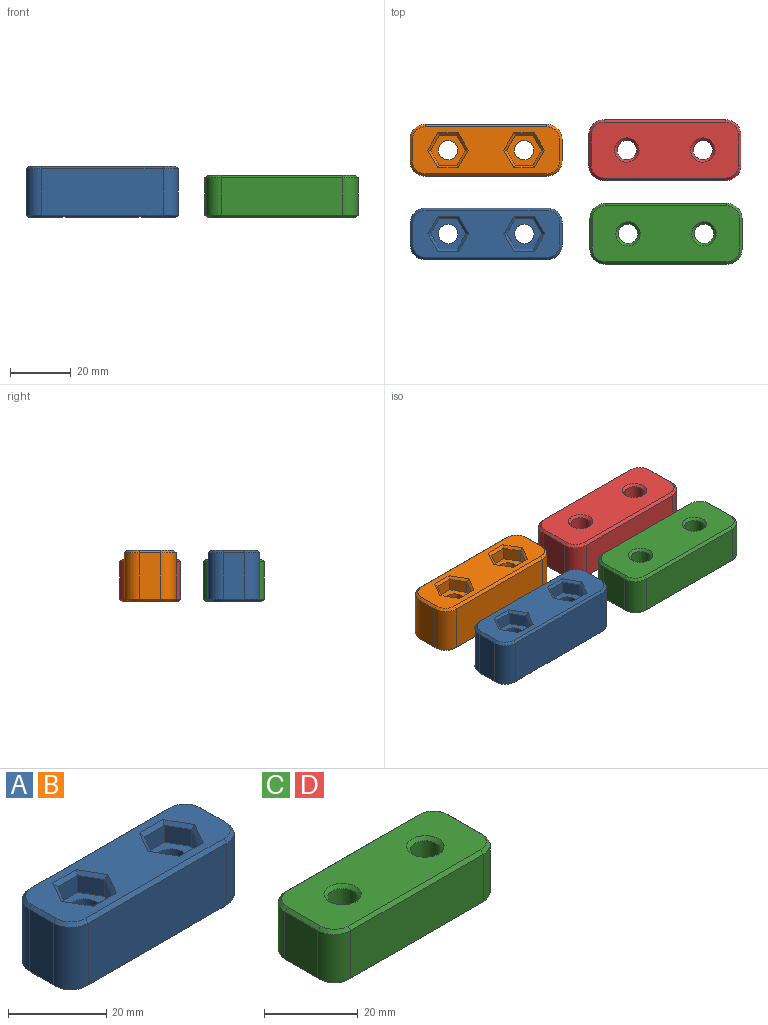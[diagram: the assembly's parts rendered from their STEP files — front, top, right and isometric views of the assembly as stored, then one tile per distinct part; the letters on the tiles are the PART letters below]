
ASSEMBLY  parts=4 mates=3
PART A: 62 faces, bbox 50x17x17 mm
  f0: plane 15.4x8.6mm, normal (0,0,-1), area 66.9mm2, adj f53,f57,f58,f59,f60,f61
  f1: plane 15.4x8.6mm, normal (0,0,-1), area 66.9mm2, adj f52,f54,f55,f56,f57,f58
  f2: cylinder r=3.2mm len=6.4mm, axis (0,0,-1), area 100.5mm2, adj f11,f27
  f3: cylinder r=3.2mm len=6.4mm, axis (0,0,-1), area 100.5mm2, adj f13,f20
  f4: plane 40x15.4mm, normal (0,1,0), area 616mm2, adj f28,f31,f35,f57
  f5: plane 15.4x7mm, normal (-1,0,0), area 107.8mm2, adj f28,f29,f32,f52
  f6: plane 40x15.4mm, normal (0,-1,0), area 616mm2, adj f29,f30,f36,f58
  f7: plane 15.4x7mm, normal (1,0,0), area 107.8mm2, adj f30,f31,f39,f61
  f8: plane 48.4x15.4mm, normal (0,0,1), area 497.2mm2, adj f32,f33,f34,f35,f36,f37,f38,f39
  f9: plane 18.8x15.4mm, normal (0,0,-1), area 173.6mm2, adj f53,f55,f57,f58
  f10: cylinder r=7.5mm len=15mm, axis (0,0,-1), area 292.2mm2, adj f11,f55
  f11: plane 15x15mm, normal (0,0,-1), area 144.5mm2, adj f2,f10
  f12: cylinder r=7.5mm len=15mm, axis (0,0,-1), area 292.2mm2, adj f13,f53
  f13: plane 15x15mm, normal (0,0,-1), area 144.5mm2, adj f3,f12
  f14: plane 5x4.2mm, normal (-0.87,-0.5,0), area 24.2mm2, adj f15,f19,f20,f45
  f15: plane 5.77x4.2mm, normal (0,-1,0), area 24.2mm2, adj f14,f16,f20,f44
  f16: plane 5x4.2mm, normal (0.87,-0.5,0), area 24.2mm2, adj f15,f17,f20,f42
  f17: plane 5x4.2mm, normal (0.87,0.5,0), area 24.2mm2, adj f16,f18,f20,f40
  f18: plane 5.77x4.2mm, normal (0,1,0), area 24.2mm2, adj f17,f19,f20,f41
  f19: plane 5x4.2mm, normal (-0.87,0.5,0), area 24.2mm2, adj f14,f18,f20,f43
  f20: plane 11.55x10mm, normal (0,0,1), area 54.4mm2, adj f3,f14,f15,f16,f17,f18,f19
  f21: plane 5x4.2mm, normal (-0.87,-0.5,0), area 24.2mm2, adj f22,f26,f27,f51
  f22: plane 5.77x4.2mm, normal (0,-1,0), area 24.2mm2, adj f21,f23,f27,f50
  f23: plane 5x4.2mm, normal (0.87,-0.5,0), area 24.2mm2, adj f22,f24,f27,f48
  f24: plane 5x4.2mm, normal (0.87,0.5,0), area 24.2mm2, adj f23,f25,f27,f46
  f25: plane 5.77x4.2mm, normal (0,1,0), area 24.2mm2, adj f24,f26,f27,f47
  f26: plane 5x4.2mm, normal (-0.87,0.5,0), area 24.2mm2, adj f21,f25,f27,f49
  f27: plane 11.55x10mm, normal (0,0,1), area 54.4mm2, adj f2,f21,f22,f23,f24,f25,f26
  f28: cylinder r=5mm len=15.4mm, axis (0,0,1), area 121mm2, adj f4,f5,f33,f54
  f29: cylinder r=5mm len=15.4mm, axis (0,0,-1), area 121mm2, adj f5,f6,f34,f56
  f30: cylinder r=5mm len=15.4mm, axis (0,0,1), area 121mm2, adj f6,f7,f38,f60
  f31: cylinder r=5mm len=15.4mm, axis (0,0,-1), area 121mm2, adj f4,f7,f37,f59
  f32: plane 7x0.8mm, normal (-0.71,0,0.71), area 7.9mm2, adj f5,f8,f33,f34
  f33: cone r=4.2mm half-angle=45deg, axis (0,0,-1), area 8.2mm2, adj f8,f28,f32,f35
  f34: cone r=4.2mm half-angle=45deg, axis (0,0,-1), area 8.2mm2, adj f8,f29,f32,f36
  f35: plane 40x0.8mm, normal (0,0.71,0.71), area 45.3mm2, adj f4,f8,f33,f37
  f36: plane 40x0.8mm, normal (0,-0.71,0.71), area 45.3mm2, adj f6,f8,f34,f38
  f37: cone r=4.2mm half-angle=45deg, axis (0,0,-1), area 8.2mm2, adj f8,f31,f35,f39
  f38: cone r=4.2mm half-angle=45deg, axis (0,0,-1), area 8.2mm2, adj f8,f30,f36,f39
  f39: plane 7x0.8mm, normal (0.71,0,0.71), area 7.9mm2, adj f7,f8,f37,f38
  f40: plane 5.8x3.81mm, normal (0.61,0.35,0.71), area 7.1mm2, adj f8,f17,f41,f42
  f41: plane 6.7x0.8mm, normal (0,0.71,0.71), area 7.1mm2, adj f8,f18,f40,f43
  f42: plane 5.8x3.81mm, normal (0.61,-0.35,0.71), area 7.1mm2, adj f8,f16,f40,f44
  f43: plane 5.8x3.81mm, normal (-0.61,0.35,0.71), area 7.1mm2, adj f8,f19,f41,f45
  f44: plane 6.7x0.8mm, normal (0,-0.71,0.71), area 7.1mm2, adj f8,f15,f42,f45
  f45: plane 5.8x3.81mm, normal (-0.61,-0.35,0.71), area 7.1mm2, adj f8,f14,f43,f44
  f46: plane 5.8x3.81mm, normal (0.61,0.35,0.71), area 7.1mm2, adj f8,f24,f47,f48
  f47: plane 6.7x0.8mm, normal (0,0.71,0.71), area 7.1mm2, adj f8,f25,f46,f49
  f48: plane 5.8x3.81mm, normal (0.61,-0.35,0.71), area 7.1mm2, adj f8,f23,f46,f50
  f49: plane 5.8x3.81mm, normal (-0.61,0.35,0.71), area 7.1mm2, adj f8,f26,f47,f51
  f50: plane 6.7x0.8mm, normal (0,-0.71,0.71), area 7.1mm2, adj f8,f22,f48,f51
  f51: plane 5.8x3.81mm, normal (-0.61,-0.35,0.71), area 7.1mm2, adj f8,f21,f49,f50
  f52: plane 7x0.8mm, normal (-0.71,0,-0.71), area 7.9mm2, adj f1,f5,f54,f56
  f53: cone r=8.3mm half-angle=45deg, axis (0,0,-1), area 52.6mm2, adj f0,f9,f12,f57,f58
  f54: cone r=4.2mm half-angle=45deg, axis (0,0,1), area 8.2mm2, adj f1,f28,f52,f57
  f55: cone r=8.3mm half-angle=45deg, axis (0,0,-1), area 52.6mm2, adj f1,f9,f10,f57,f58
  f56: cone r=4.2mm half-angle=45deg, axis (0,0,1), area 8.2mm2, adj f1,f29,f52,f58
  f57: plane 40x0.81mm, normal (0,0.71,-0.71), area 41.7mm2, adj f0,f1,f4,f9,f53,f54,f55,f59
  f58: plane 40x0.8mm, normal (0,-0.71,-0.71), area 41.7mm2, adj f0,f1,f6,f9,f53,f55,f56,f60
  f59: cone r=4.2mm half-angle=45deg, axis (0,0,1), area 8.2mm2, adj f0,f31,f57,f61
  f60: cone r=4.2mm half-angle=45deg, axis (0,0,1), area 8.2mm2, adj f0,f30,f58,f61
  f61: plane 7x0.8mm, normal (0.71,0,-0.71), area 7.9mm2, adj f0,f7,f59,f60
PART B: same geometry as A
PART C: 32 faces, bbox 50x20x14 mm
  f0: plane 40x12.4mm, normal (0,1,0), area 496mm2, adj f8,f11,f15,f25
  f1: plane 12.4x10mm, normal (-1,0,0), area 124mm2, adj f8,f9,f12,f22
  f2: plane 40x12.4mm, normal (0,-1,0), area 496mm2, adj f9,f10,f16,f26
  f3: cylinder r=3.2mm len=12.4mm, axis (0,0,-1), area 249.3mm2, adj f21,f31
  f4: cylinder r=3.2mm len=12.4mm, axis (0,0,-1), area 249.3mm2, adj f20,f30
  f5: plane 12.4x10mm, normal (1,0,0), area 124mm2, adj f10,f11,f19,f29
  f6: plane 48.4x18.4mm, normal (0,0,1), area 774.9mm2, adj f22,f23,f24,f25,f26,f27,f28,f29
  f7: plane 48.4x18.4mm, normal (0,0,-1), area 774.9mm2, adj f12,f13,f14,f15,f16,f17,f18,f19
  f8: cylinder r=5mm len=12.4mm, axis (0,0,1), area 97.4mm2, adj f0,f1,f13,f23
  f9: cylinder r=5mm len=12.4mm, axis (0,0,-1), area 97.4mm2, adj f1,f2,f14,f24
  f10: cylinder r=5mm len=12.4mm, axis (0,0,1), area 97.4mm2, adj f2,f5,f18,f28
  f11: cylinder r=5mm len=12.4mm, axis (0,0,-1), area 97.4mm2, adj f0,f5,f17,f27
  f12: plane 10x0.8mm, normal (-0.71,0,-0.71), area 11.3mm2, adj f1,f7,f13,f14
  f13: cone r=4.2mm half-angle=45deg, axis (0,0,1), area 8.2mm2, adj f7,f8,f12,f15
  f14: cone r=4.2mm half-angle=45deg, axis (0,0,1), area 8.2mm2, adj f7,f9,f12,f16
  f15: plane 40x0.8mm, normal (0,0.71,-0.71), area 45.3mm2, adj f0,f7,f13,f17
  f16: plane 40x0.8mm, normal (0,-0.71,-0.71), area 45.3mm2, adj f2,f7,f14,f18
  f17: cone r=4.2mm half-angle=45deg, axis (0,0,1), area 8.2mm2, adj f7,f11,f15,f19
  f18: cone r=4.2mm half-angle=45deg, axis (0,0,1), area 8.2mm2, adj f7,f10,f16,f19
  f19: plane 10x0.8mm, normal (0.71,0,-0.71), area 11.3mm2, adj f5,f7,f17,f18
  f20: cone r=4mm half-angle=45deg, axis (0,0,-1), area 25.6mm2, adj f4,f7
  f21: cone r=4mm half-angle=45deg, axis (0,0,-1), area 25.6mm2, adj f3,f7
  f22: plane 10x0.8mm, normal (-0.71,0,0.71), area 11.3mm2, adj f1,f6,f23,f24
  f23: cone r=4.2mm half-angle=45deg, axis (0,0,-1), area 8.2mm2, adj f6,f8,f22,f25
  f24: cone r=4.2mm half-angle=45deg, axis (0,0,-1), area 8.2mm2, adj f6,f9,f22,f26
  f25: plane 40x0.8mm, normal (0,0.71,0.71), area 45.3mm2, adj f0,f6,f23,f27
  f26: plane 40x0.8mm, normal (0,-0.71,0.71), area 45.3mm2, adj f2,f6,f24,f28
  f27: cone r=4.2mm half-angle=45deg, axis (0,0,-1), area 8.2mm2, adj f6,f11,f25,f29
  f28: cone r=4.2mm half-angle=45deg, axis (0,0,-1), area 8.2mm2, adj f6,f10,f26,f29
  f29: plane 10x0.8mm, normal (0.71,0,0.71), area 11.3mm2, adj f5,f6,f27,f28
  f30: cone r=3.2mm half-angle=45deg, axis (0,0,1), area 25.6mm2, adj f4,f6
  f31: cone r=3.2mm half-angle=45deg, axis (0,0,1), area 25.6mm2, adj f3,f6
PART D: same geometry as C
PLACE A t=(-29.23,-13.54,-13.5)mm
PLACE B t=(-29.31,13.98,-13.5)mm
PLACE C t=(29.86,-13.51,-13.5)mm
PLACE D t=(29.5,14.02,-13.5)mm
MATE planar C.f7 <-> D.f7  axis (0,0,-1) through (29.86,-13.51,-13.5)mm
MATE planar C.f7 <-> B.f9  axis (0,0,-1) through (29.86,-13.51,-13.5)mm
MATE planar C.f7 <-> A.f9  axis (0,0,-1) through (29.86,-13.51,-13.5)mm
